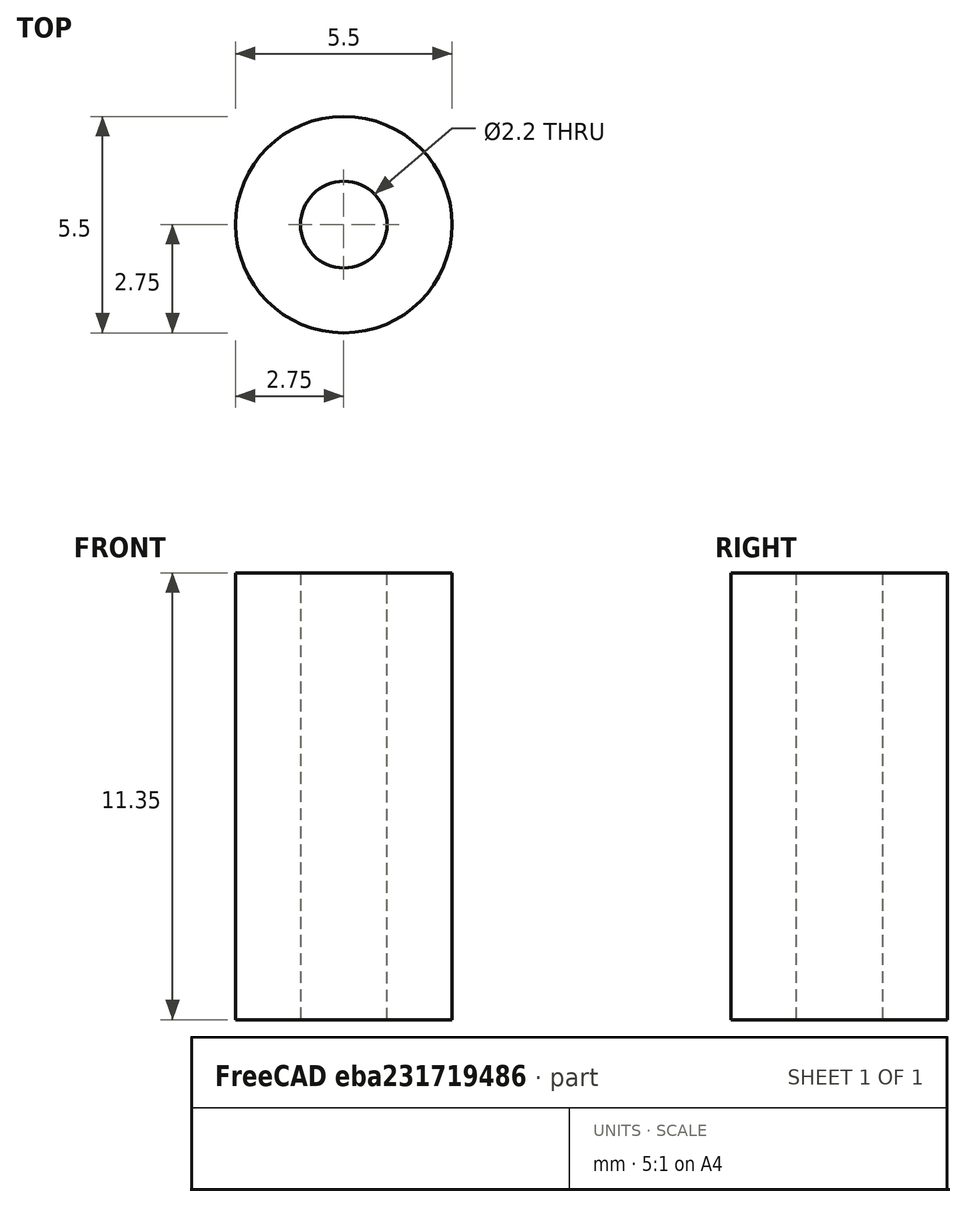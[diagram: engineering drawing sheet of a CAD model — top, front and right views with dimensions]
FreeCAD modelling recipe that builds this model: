
FCSTD DOCUMENT  (FreeCAD 0.18R13959 (Git))
Label: Spacer_M2x11.35mm
License: CreativeCommons Attribution-NonCommercial-ShareAlike
LicenseURL: http://creativecommons.org/licenses/by-nc-sa/4.0/
objects: Sketcher::SketchObject×1, PartDesign::Pad×1, PartDesign::Body×1, Mesh::Feature×1
note: 4 computed .brp shape members not serialized (recipe doc carries the construction recipe); baked Part::Feature solids carry a one-line shape summary decoded from their .brp

FEATURE [Sketcher::SketchObject] Sketch
  MapMode = 5
  Support = -> [XY_Plane]
  sketch-geometry (2):
    g0: Circle CenterX=0 CenterY=0 CenterZ=0 NormalX=0 NormalY=0 NormalZ=1 AngleXU=0 Radius=2.75
    g1: Circle CenterX=0 CenterY=0 CenterZ=0 NormalX=0 NormalY=0 NormalZ=1 AngleXU=0 Radius=1.1
  constraints (4):
    c: Coincident(g0,g-1)
    c: Radius(g0) = 2.75
    c: Coincident(g1,g-1)
    c: Radius(g1) = 1.1
FEATURE [PartDesign::Pad] Pad
  Length = 11.35
  Length2 = 100
  Profile = -> Sketch
  Type = 0
FEATURE [PartDesign::Body] Body
  Group = -> [Sketch,Pad]
  Origin = -> Origin
  Tip = -> Pad
FEATURE [Mesh::Feature] Mesh  label="Pad (Meshed)"
